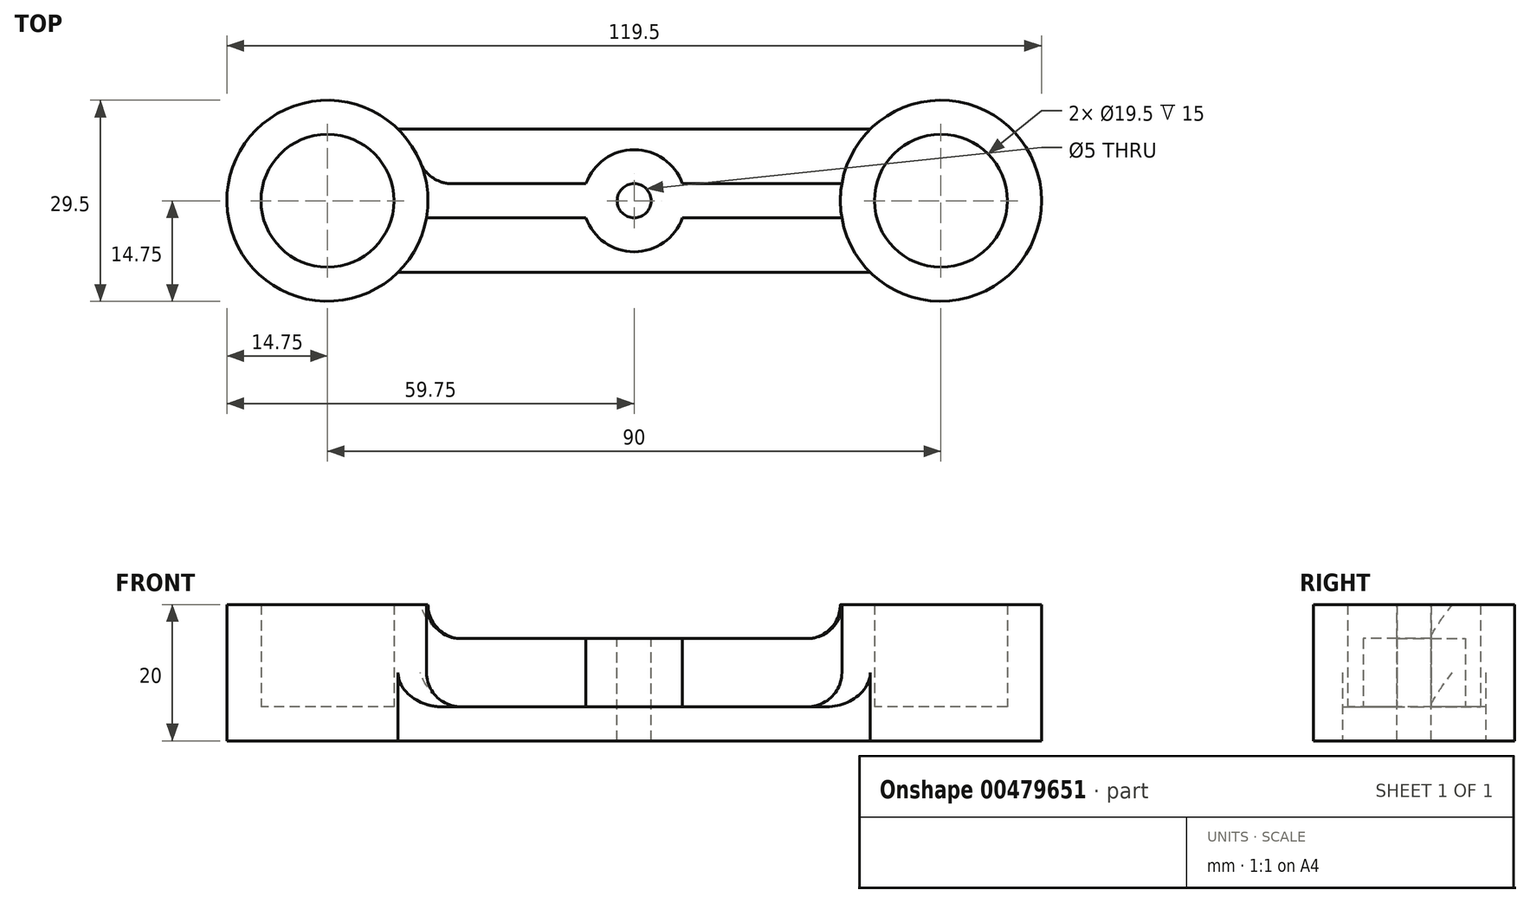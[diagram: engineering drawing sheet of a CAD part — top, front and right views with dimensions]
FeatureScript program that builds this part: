
annotation { "Feature Type Name" : "Feature", "Feature Type Description" : "" }
export const myFeature = defineFeature(function(context is Context, id is Id, definition is map)
    precondition{}
    {
        {
            var Q0;
            Q0=qCreatedBy(makeId("Top.planeOp"),FACE);
            var sketch = newSketch(context, id + "F0", { "sketchPlane" : qUnion([Q0])});
            skLineSegment(sketch, "E0.bottom", {"start": v(45, 9.75) * mm, "end": v(-45, 9.75) * mm});
            skLineSegment(sketch, "E0.top", {"start": v(45, -9.75) * mm, "end": v(-45, -9.75) * mm});
            skPoint(sketch, "E0.middle", {"position": v(0, 0) * mm});
            skCircle(sketch, "E1", {"center": v(-45, 0) * mm, "radius": 9.75 * mm});
            skCircle(sketch, "E2.0", {"center": v(-45, 0) * mm, "radius": 14.75 * mm});
            skCircle(sketch, "E3.MirrorC", {"center": v(45, 0) * mm, "radius": 14.75 * mm});
            skCircle(sketch, "E4.MirrorC", {"center": v(45, 0) * mm, "radius": 9.75 * mm});
            skSolve(sketch);
        }
        {
            var Q0;
            {var subQ0=sQuery(id+"F0.wireOp",EDGE,"E1");var subQ1=sQuery(id+"F0.wireOp",EDGE,"E0.bottom");var subQ2=makeQuery(id+"F0.imprint","INTERSECT",VERTEX,{"derivedFrom":[subQ1,subQ0]});Q0=makeQuery(id+"F0.imprint","IMPRINT",FACE,{"disambiguationData":[TD([[makeQuery(id+"F0.imprint","IMPRINT",EDGE,{"disambiguationData":[TD([[subQ2,1.0]])],"derivedFrom":subQ1}),-1.0]])]});}
            var Q1;
            {var subQ0=sQuery(id+"F0.wireOp",EDGE,"E1");var subQ1=sQuery(id+"F0.wireOp",EDGE,"E0.bottom");var subQ2=makeQuery(id+"F0.imprint","INTERSECT",VERTEX,{"derivedFrom":[subQ1,subQ0]});Q1=makeQuery(id+"F0.imprint","IMPRINT",FACE,{"disambiguationData":[TD([[makeQuery(id+"F0.imprint","IMPRINT",EDGE,{"disambiguationData":[TD([[subQ2,1.0]])],"derivedFrom":subQ1}),1.0]])]});}
            var Q2;
            {var subQ0=sQuery(id+"F0.wireOp",EDGE,"E4.MirrorC");var subQ1=sQuery(id+"F0.wireOp",EDGE,"E0.bottom");var subQ2=makeQuery(id+"F0.imprint","INTERSECT",VERTEX,{"derivedFrom":[subQ1,subQ0]});Q2=makeQuery(id+"F0.imprint","IMPRINT",FACE,{"disambiguationData":[TD([[makeQuery(id+"F0.imprint","IMPRINT",EDGE,{"disambiguationData":[TD([[subQ2,-1.0]])],"derivedFrom":subQ1}),1.0]])]});}
            var Q3;
            {var subQ0=sQuery(id+"F0.wireOp",EDGE,"E4.MirrorC");var subQ1=sQuery(id+"F0.wireOp",EDGE,"E0.bottom");var subQ2=makeQuery(id+"F0.imprint","INTERSECT",VERTEX,{"derivedFrom":[subQ1,subQ0]});Q3=makeQuery(id+"F0.imprint","IMPRINT",FACE,{"disambiguationData":[TD([[makeQuery(id+"F0.imprint","IMPRINT",EDGE,{"disambiguationData":[TD([[subQ2,-1.0]])],"derivedFrom":subQ1}),-1.0]])]});}
            extrude(context, id + "F1", {"entities" : qUnion([Q0, Q1, Q2, Q3]), "depth" : 20 * mm, "offsetDistance" : 25 * mm});
        }
        {
            var Q0;
            Q0=qCreatedBy(makeId("Top.planeOp"),FACE);
            var sketch = newSketch(context, id + "F2", { "sketchPlane" : qUnion([Q0])});
            skLineSegment(sketch, "E5.bottom", {"start": v(-55, 10.5) * mm, "end": v(55, 10.5) * mm});
            skLineSegment(sketch, "E5.top", {"start": v(-55, -10.5) * mm, "end": v(55, -10.5) * mm});
            skLineSegment(sketch, "E5.left", {"start": v(-55, 10.5) * mm, "end": v(-55, -10.5) * mm});
            skLineSegment(sketch, "E5.right", {"start": v(55, 10.5) * mm, "end": v(55, -10.5) * mm});
            skPoint(sketch, "E5.middle", {"position": v(0, 0) * mm});
            skSolve(sketch);
        }
        {
            var Q0;
            Q0=makeQuery(id+"F2.imprint","IMPRINT",FACE,{"disambiguationData":[TD([[makeQuery(id+"F2.imprint","IMPRINT",EDGE,{"derivedFrom":sQuery(id+"F2.wireOp",EDGE,"E5.bottom")}),-1.0]])]});
            extrude(context, id + "F3", {"entities" : qUnion([Q0]), "depth" : 5 * mm, "offsetDistance" : 25 * mm});
        }
        {
            var Q0;
            Q0=qCreatedBy(makeId("Top.planeOp"),FACE);
            var sketch = newSketch(context, id + "F4", { "sketchPlane" : qUnion([Q0])});
            skLineSegment(sketch, "E6.bottom", {"start": v(34, -2.5) * mm, "end": v(-34, -2.5) * mm});
            skLineSegment(sketch, "E6.top", {"start": v(34, 2.5) * mm, "end": v(-34, 2.5) * mm});
            skLineSegment(sketch, "E6.left", {"start": v(34, -2.5) * mm, "end": v(34, 2.5) * mm});
            skLineSegment(sketch, "E6.right", {"start": v(-34, -2.5) * mm, "end": v(-34, 2.5) * mm});
            skPoint(sketch, "E6.middle", {"position": v(0, 0) * mm});
            skSolve(sketch);
        }
        {
            var Q0;
            Q0=makeQuery(id+"F4.imprint","IMPRINT",FACE,{"disambiguationData":[TD([[makeQuery(id+"F4.imprint","IMPRINT",EDGE,{"derivedFrom":sQuery(id+"F4.wireOp",EDGE,"E6.bottom")}),-1.0]])]});
            extrude(context, id + "F5", {"entities" : qUnion([Q0]), "depth" : 15 * mm, "offsetDistance" : 25 * mm});
        }
        {
            var Q0;
            Q0=makeQuery(id+"F5.opExtrude","SWEPT_BODY",BODY,{"disambiguationData":[OSD([sQuery(id+"F4.wireOp",EDGE,"E6.bottom"),sQuery(id+"F4.wireOp",EDGE,"E6.top"),sQuery(id+"F4.wireOp",EDGE,"E6.left"),sQuery(id+"F4.wireOp",EDGE,"E6.right")])]});
            var Q1;
            Q1=makeQuery(id+"F1.opExtrude","SWEPT_BODY",BODY,{"disambiguationData":[OSD([sQuery(id+"F0.wireOp",EDGE,"E3.MirrorC"),sQuery(id+"F0.wireOp",EDGE,"E4.MirrorC")])]});
            var Q2;
            Q2=makeQuery(id+"F3.opExtrude","SWEPT_BODY",BODY,{"disambiguationData":[OSD([sQuery(id+"F2.wireOp",EDGE,"E5.bottom"),sQuery(id+"F2.wireOp",EDGE,"E5.top"),sQuery(id+"F2.wireOp",EDGE,"E5.left"),sQuery(id+"F2.wireOp",EDGE,"E5.right")])]});
            var Q3;
            Q3=makeQuery(id+"F1.opExtrude","SWEPT_BODY",BODY,{"disambiguationData":[OSD([sQuery(id+"F0.wireOp",EDGE,"E1"),sQuery(id+"F0.wireOp",EDGE,"E2.0")])]});
            booleanBodies(context, id + "F6", {"operationType" : BooleanOperationType.UNION, "tools" : qUnion([Q0, Q1, Q2, Q3])});
        }
        {
            var Q0;
            Q0=makeQuery(id+"F6.opBoolean","INTERSECT",EDGE,{"derivedFrom":[makeQuery(id+"F1.opExtrude","SWEPT_FACE",FACE,{"disambiguationData":[OSD([sQuery(id+"F0.wireOp",EDGE,"E2.0")])]}),makeQuery(id+"F5.opExtrude","SWEPT_FACE",FACE,{"disambiguationData":[OSD([sQuery(id+"F4.wireOp",EDGE,"E6.top")])]})]});
            var Q1;
            Q1=makeQuery(id+"F6.opBoolean","INTERSECT",EDGE,{"disambiguationData":[OD(0.0)],"derivedFrom":[makeQuery(id+"F1.opExtrude","SWEPT_FACE",FACE,{"disambiguationData":[OSD([sQuery(id+"F0.wireOp",EDGE,"E2.0")])]}),makeQuery(id+"F3.opExtrude","CAP_FACE",FACE,{"disambiguationData":[OSD([sQuery(id+"F2.wireOp",EDGE,"E5.bottom"),sQuery(id+"F2.wireOp",EDGE,"E5.top"),sQuery(id+"F2.wireOp",EDGE,"E5.left"),sQuery(id+"F2.wireOp",EDGE,"E5.right")])],"isStart":false})]});
            var Q2;
            Q2=makeQuery(id+"F6.opBoolean","INTERSECT",EDGE,{"disambiguationData":[OD(1.0)],"derivedFrom":[makeQuery(id+"F1.opExtrude","SWEPT_FACE",FACE,{"disambiguationData":[OSD([sQuery(id+"F0.wireOp",EDGE,"E2.0")])]}),makeQuery(id+"F3.opExtrude","CAP_FACE",FACE,{"disambiguationData":[OSD([sQuery(id+"F2.wireOp",EDGE,"E5.bottom"),sQuery(id+"F2.wireOp",EDGE,"E5.top"),sQuery(id+"F2.wireOp",EDGE,"E5.left"),sQuery(id+"F2.wireOp",EDGE,"E5.right")])],"isStart":false})]});
            var Q3;
            Q3=makeQuery(id+"F6.opBoolean","INTERSECT",EDGE,{"derivedFrom":[makeQuery(id+"F1.opExtrude","SWEPT_FACE",FACE,{"disambiguationData":[OSD([sQuery(id+"F0.wireOp",EDGE,"E2.0")])]}),makeQuery(id+"F5.opExtrude","CAP_FACE",FACE,{"disambiguationData":[OSD([sQuery(id+"F4.wireOp",EDGE,"E6.bottom"),sQuery(id+"F4.wireOp",EDGE,"E6.top"),sQuery(id+"F4.wireOp",EDGE,"E6.left"),sQuery(id+"F4.wireOp",EDGE,"E6.right")])],"isStart":false})]});
            var Q4;
            Q4=makeQuery(id+"F6.opBoolean","INTERSECT",EDGE,{"disambiguationData":[OD(1.0)],"derivedFrom":[makeQuery(id+"F1.opExtrude","SWEPT_FACE",FACE,{"disambiguationData":[OSD([sQuery(id+"F0.wireOp",EDGE,"E3.MirrorC")])]}),makeQuery(id+"F3.opExtrude","CAP_FACE",FACE,{"disambiguationData":[OSD([sQuery(id+"F2.wireOp",EDGE,"E5.bottom"),sQuery(id+"F2.wireOp",EDGE,"E5.top"),sQuery(id+"F2.wireOp",EDGE,"E5.left"),sQuery(id+"F2.wireOp",EDGE,"E5.right")])],"isStart":false})]});
            var Q5;
            Q5=makeQuery(id+"F6.opBoolean","INTERSECT",EDGE,{"derivedFrom":[makeQuery(id+"F1.opExtrude","SWEPT_FACE",FACE,{"disambiguationData":[OSD([sQuery(id+"F0.wireOp",EDGE,"E3.MirrorC")])]}),makeQuery(id+"F5.opExtrude","CAP_FACE",FACE,{"disambiguationData":[OSD([sQuery(id+"F4.wireOp",EDGE,"E6.bottom"),sQuery(id+"F4.wireOp",EDGE,"E6.top"),sQuery(id+"F4.wireOp",EDGE,"E6.left"),sQuery(id+"F4.wireOp",EDGE,"E6.right")])],"isStart":false})]});
            var Q6;
            Q6=makeQuery(id+"F6.opBoolean","INTERSECT",EDGE,{"disambiguationData":[OD(0.0)],"derivedFrom":[makeQuery(id+"F1.opExtrude","SWEPT_FACE",FACE,{"disambiguationData":[OSD([sQuery(id+"F0.wireOp",EDGE,"E3.MirrorC")])]}),makeQuery(id+"F3.opExtrude","CAP_FACE",FACE,{"disambiguationData":[OSD([sQuery(id+"F2.wireOp",EDGE,"E5.bottom"),sQuery(id+"F2.wireOp",EDGE,"E5.top"),sQuery(id+"F2.wireOp",EDGE,"E5.left"),sQuery(id+"F2.wireOp",EDGE,"E5.right")])],"isStart":false})]});
            fillet(context, id + "F7", {"entities" : qUnion([Q0, Q1, Q2, Q3, Q4, Q5, Q6]), "radius" : 5 * mm, "tangentPropagation" : true, "allowEdgeOverflow" : false});
        }
        {
            var Q0;
            Q0=qCreatedBy(makeId("Top.planeOp"),FACE);
            var sketch = newSketch(context, id + "F8", { "sketchPlane" : qUnion([Q0])});
            skCircle(sketch, "E7", {"center": v(0, 0) * mm, "radius": 7.5 * mm});
            skLineSegment(sketch, "E8", {"start": v(5.38, -19.98) * mm, "end": v(7.98, -24.09) * mm});
            skSolve(sketch);
        }
        {
            var Q0;
            Q0=makeQuery(id+"F8.imprint","IMPRINT",FACE,{"disambiguationData":[TD([[makeQuery(id+"F8.imprint","IMPRINT",EDGE,{"derivedFrom":sQuery(id+"F8.wireOp",EDGE,"E7")}),1.0]])]});
            extrude(context, id + "F9", {"entities" : qUnion([Q0]), "operationType" : NewBodyOperationType.ADD, "depth" : 15 * mm, "offsetDistance" : 25 * mm});
        }
        {
            var Q0;
            Q0=makeQuery(id+"F9.boolean.opBoolean","MERGE",FACE,{"derivedFrom":[makeQuery(id+"F5.opExtrude","CAP_FACE",FACE,{"disambiguationData":[OSD([sQuery(id+"F4.wireOp",EDGE,"E6.bottom"),sQuery(id+"F4.wireOp",EDGE,"E6.top"),sQuery(id+"F4.wireOp",EDGE,"E6.left"),sQuery(id+"F4.wireOp",EDGE,"E6.right")])],"isStart":false}),makeQuery(id+"F9.opExtrude","CAP_FACE",FACE,{"disambiguationData":[OSD([sQuery(id+"F8.wireOp",EDGE,"E7")])],"isStart":false})]});
            var sketch = newSketch(context, id + "F10", { "sketchPlane" : qUnion([Q0])});
            skPoint(sketch, "E9", {"position": v(0, 0) * mm});
            skSolve(sketch);
        }
        {
            var Q0;
            Q0=sQuery(id+"F10.wireOp",VERTEX,"E9");
            var Q1;
            Q1=makeQuery(id+"F5.opExtrude","SWEPT_BODY",BODY,{"disambiguationData":[OSD([sQuery(id+"F4.wireOp",EDGE,"E6.bottom"),sQuery(id+"F4.wireOp",EDGE,"E6.top"),sQuery(id+"F4.wireOp",EDGE,"E6.left"),sQuery(id+"F4.wireOp",EDGE,"E6.right")])]});
            hole(context, id + "F11", {"style" : HoleStyle.SIMPLE, "endStyle" : HoleEndStyle.THROUGH, "standardTappedOrClearance" : lookupTablePath({ "standard" : "ISO", "engagement" : "75%", "pitch" : "1 mm", "size" : "M6", "type" : "Tapped" }), "standardBlindInLast" : lookupTablePath({ "standard" : "ISO", "engagement" : "75%", "pitch" : "1 mm", "size" : "M6", "type" : "Tapped" }), "holeDiameter" : 5 * mm, "majorDiameter" : 6 * mm, "showTappedDepth" : true, "isTappedThrough" : true, "tappedDepth" : 12 * mm, "tapClearance" : 3, "startFromSketch" : true, "locations" : qUnion([Q0]), "scope" : qUnion([Q1])});
        }
    });
